# Revit family: EVAN WBI Теплоаккумулятор буферный бак 300-2000 л - 1
name_source: partatom
category: Оборудование
units: mm (PartAtom-declared; Revit-internal decimal feet)

## family parameters
Всегда вертикально = Да
Классификация = Нет
На основе рабочей плоскости = Нет
Общий = Нет
При загрузке вырезать с полостями = Нет
Размер круглого соединителя = Использовать диаметр
Тип детали = Нормальный
Точка расчета площади = Нет

## types (7) — shared parameters
ADSK_Классификация нагрузок = Прочее
ADSK_Количество фаз = 1
ADSK_Коэффициент мощности = 1
ADSK_Материал = Конструкционная сталь
ADSK_Напряжение = 0 В
ADSK_Номинальная мощность = 0 Вт
ADSK_Полная мощность = 0 кВт
D2_colp = 23 мм
Dкороба = 20 мм
G1ext = 46 мм
G1int = 30 мм
G2ext = 22 мм
G2int = 24 мм
H7 = 864 мм
N1 = 40 мм
N2 = 16 мм
N3 = 32 мм
N4 = 40 мм
URL = https://www.evan.ru
База = Бойлер косвенного нагрева напольный
Высота 1 = 20 мм
Материал корпуса = Конструкционная сталь
Пластик прозрачный = Пластик_прозрачный
Пластик_красный = Пластик_красный
Пластик_синий = Пластик_синий
Пластмасса_черная = Пластмасса_черная
Серый = Серый
Стекло = Стекло

## per-type parameters (varying)
| type | D | H3 | H5 | Диаметр1 | Диаметр2 | Объем, л |
| Теплоаккумулятор / буферный бак EVAN WBI 300 | 590 мм | 683 мм | 1613 мм | 289 мм | 289 мм | 300 |
| Теплоаккумулятор / буферный бак EVAN WBI 400 | 750 мм | 548 мм | 1148 мм | 369 мм | 369 мм | 400 |
| Теплоаккумулятор / буферный бак EVAN WBI 500 | 750 мм | 666 мм | 1499 мм | 369 мм | 369 мм | 500 |
| Теплоаккумулятор / буферный бак EVAN WBI 800 | 950 мм | 595 мм | 1345 мм | 469 мм | 469 мм | 800 |
| Теплоаккумулятор / буферный бак EVAN WBI 1000 | 950 мм | 763 мм | 1696 мм | 469 мм | 469 мм | 1000 |
| Теплоаккумулятор / буферный бак EVAN WBI 1500 | 1120 мм | 853 мм | 1953 мм | 554 мм | 554 мм | 1500 |
| Теплоаккумулятор / буферный бак EVAN WBI 2000 | 1200 мм | 865 мм | 1965 мм | 594 мм | 594 мм | 2000 |
